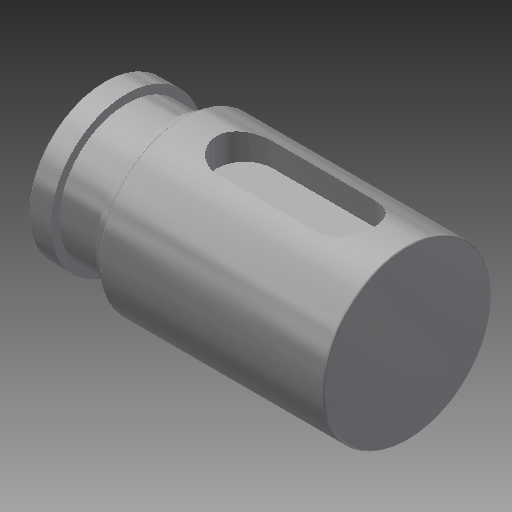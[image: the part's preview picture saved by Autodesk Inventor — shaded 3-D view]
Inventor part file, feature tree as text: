
AUTODESK INVENTOR PART (.ipt)
format: ipt  version: 2019.4 (Build 234330000, 330)  size: 210,944 bytes
history: native  units: mm
features: other x8, fillet x4
ambient origin geometry x6: Origin, XZ Plane, XY Plane, X Axis, Y Axis, Z Axis
bodies: Body1 (feature_tree)
feature tree (12):
  other  "實體1"
  other  "迴轉1"
  fillet  "圓角9"  [1 undecoded]
  fillet  "圓角10"  Radius=13.5mm
  fillet  "圓角8"  Radius=15.0mm
  fillet  "圓角4"  [1 undecoded]
  other  "鍵槽1"
  other  "扣環槽1"
  other  "起始平面"
  other  "主要草圖"
  other  "iFeature27:1"
  other  "iFeature3:1"
note: 2 required parameter values undecoded (feature->parameter linkage not recoverable at this tier; creation-order binding heuristic only, values carry confidence <= 0.55)
